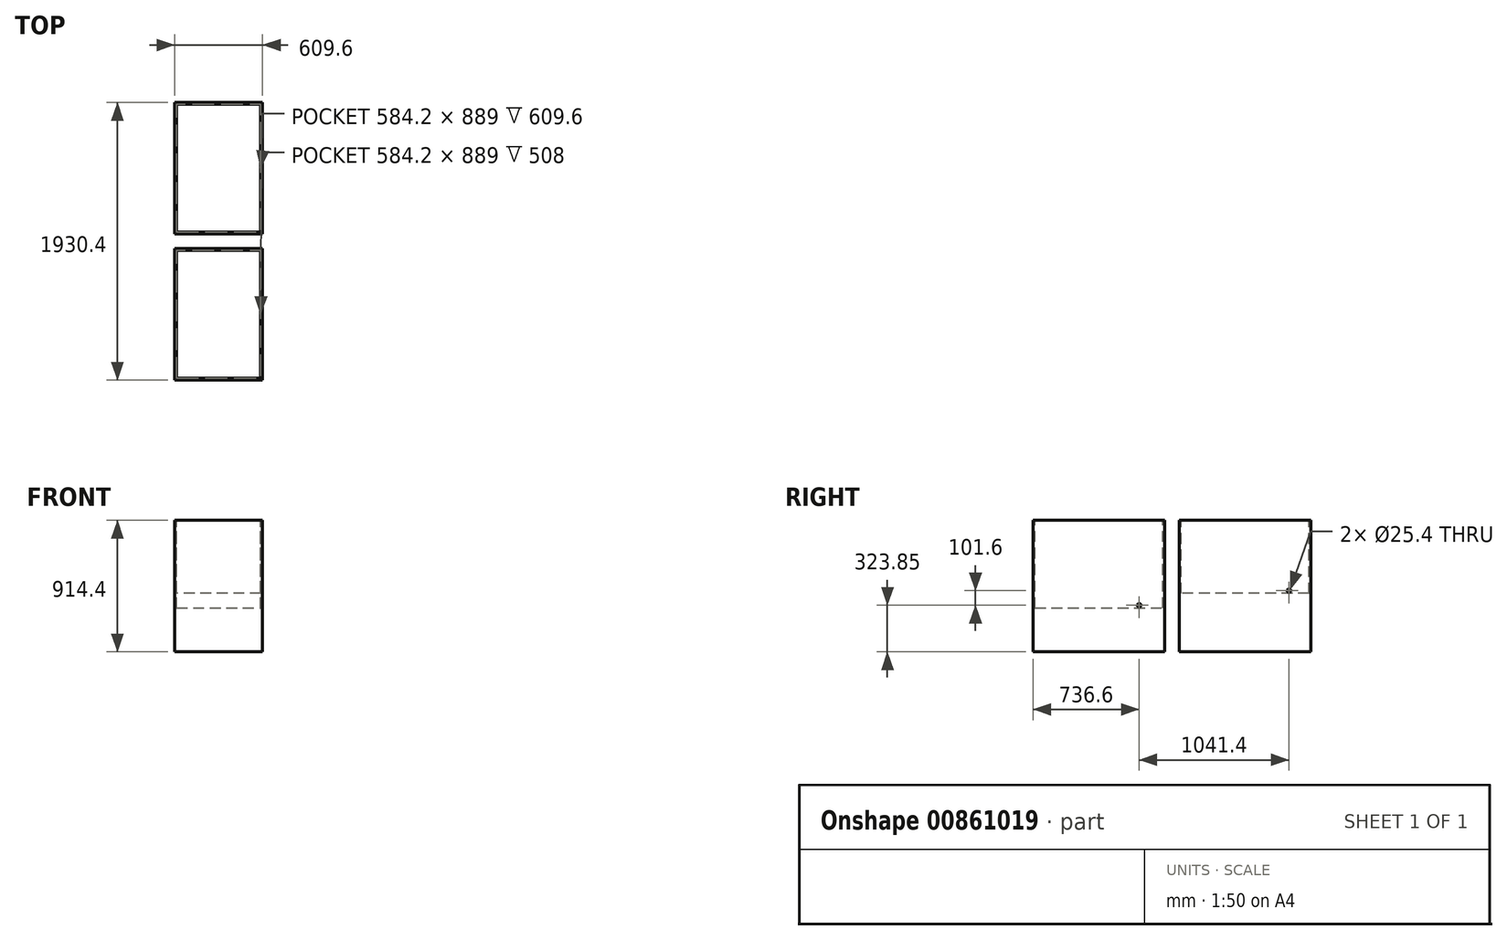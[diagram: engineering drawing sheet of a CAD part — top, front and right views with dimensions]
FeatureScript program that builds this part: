
annotation { "Feature Type Name" : "Feature", "Feature Type Description" : "" }
export const myFeature = defineFeature(function(context is Context, id is Id, definition is map)
    precondition{}
    {
        {
            var Q0;
            Q0=qCreatedBy(makeId("Top.planeOp"),FACE);
            var sketch = newSketch(context, id + "F0", { "sketchPlane" : qUnion([Q0])});
            skLineSegment(sketch, "E0.bottom", {"start": v(304.8, 457.2) * mm, "end": v(-304.8, 457.2) * mm});
            skLineSegment(sketch, "E0.top", {"start": v(304.8, -457.2) * mm, "end": v(-304.8, -457.2) * mm});
            skLineSegment(sketch, "E0.left", {"start": v(304.8, 457.2) * mm, "end": v(304.8, -457.2) * mm});
            skLineSegment(sketch, "E0.right", {"start": v(-304.8, 457.2) * mm, "end": v(-304.8, -457.2) * mm});
            skPoint(sketch, "E0.middle", {"position": v(0, 0) * mm});
            skSolve(sketch);
        }
        {
            var Q0;
            Q0=makeQuery(id+"F0.imprint","IMPRINT",FACE,{"disambiguationData":[TD([[makeQuery(id+"F0.imprint","IMPRINT",EDGE,{"derivedFrom":sQuery(id+"F0.wireOp",EDGE,"E0.bottom")}),1.0]])]});
            extrude(context, id + "F1", {"entities" : qUnion([Q0]), "depth" : 914.4 * mm, "offsetDistance" : 25.4 * mm});
        }
        {
            var Q0;
            Q0=qCreatedBy(makeId("Top.planeOp"),FACE);
            var sketch = newSketch(context, id + "F2", { "sketchPlane" : qUnion([Q0])});
            skLineSegment(sketch, "E1.bottom", {"start": v(-304.8, -558.8) * mm, "end": v(304.8, -558.8) * mm});
            skLineSegment(sketch, "E1.top", {"start": v(-304.8, -1473.2) * mm, "end": v(304.8, -1473.2) * mm});
            skLineSegment(sketch, "E1.left", {"start": v(-304.8, -558.8) * mm, "end": v(-304.8, -1473.2) * mm});
            skLineSegment(sketch, "E1.right", {"start": v(304.8, -558.8) * mm, "end": v(304.8, -1473.2) * mm});
            skSolve(sketch);
        }
        {
            var Q0;
            Q0 = qSketchRegion(id + "F2", true);
            extrude(context, id + "F3", {"entities" : qUnion([Q0]), "depth" : 914.4 * mm, "offsetDistance" : 25.4 * mm});
        }
        {
            var Q0;
            Q0=makeQuery(id+"F1.opExtrude","CAP_FACE",FACE,{"disambiguationData":[OSD([sQuery(id+"F0.wireOp",EDGE,"E0.bottom"),sQuery(id+"F0.wireOp",EDGE,"E0.top"),sQuery(id+"F0.wireOp",EDGE,"E0.left"),sQuery(id+"F0.wireOp",EDGE,"E0.right")])],"isStart":false});
            var sketch = newSketch(context, id + "F4", { "sketchPlane" : qUnion([Q0])});
            skLineSegment(sketch, "E2.bottom", {"start": v(292.1, 444.5) * mm, "end": v(-292.1, 444.5) * mm});
            skLineSegment(sketch, "E2.top", {"start": v(292.1, -444.5) * mm, "end": v(-292.1, -444.5) * mm});
            skLineSegment(sketch, "E2.left", {"start": v(292.1, 444.5) * mm, "end": v(292.1, -444.5) * mm});
            skLineSegment(sketch, "E2.right", {"start": v(-292.1, 444.5) * mm, "end": v(-292.1, -444.5) * mm});
            skPoint(sketch, "E2.middle", {"position": v(0, 0) * mm});
            skSolve(sketch);
        }
        {
            var Q0;
            Q0=makeQuery(id+"F4.imprint","IMPRINT",FACE,{"disambiguationData":[TD([[makeQuery(id+"F4.imprint","IMPRINT",EDGE,{"derivedFrom":sQuery(id+"F4.wireOp",EDGE,"E2.bottom")}),1.0]])]});
            extrude(context, id + "F5", {"entities" : qUnion([Q0]), "operationType" : NewBodyOperationType.REMOVE, "oppositeDirection" : true, "depth" : 508 * mm, "offsetDistance" : 25.4 * mm});
        }
        {
            var Q0;
            Q0=makeQuery(id+"F3.opExtrude","CAP_FACE",FACE,{"disambiguationData":[OSD([sQuery(id+"F2.wireOp",EDGE,"E1.bottom"),sQuery(id+"F2.wireOp",EDGE,"E1.top"),sQuery(id+"F2.wireOp",EDGE,"E1.left"),sQuery(id+"F2.wireOp",EDGE,"E1.right")])],"isStart":false});
            var sketch = newSketch(context, id + "F6", { "sketchPlane" : qUnion([Q0])});
            skLineSegment(sketch, "E3.bottom", {"start": v(-292.1, -1460.5) * mm, "end": v(292.1, -1460.5) * mm});
            skLineSegment(sketch, "E3.top", {"start": v(-292.1, -571.5) * mm, "end": v(292.1, -571.5) * mm});
            skLineSegment(sketch, "E3.left", {"start": v(-292.1, -1460.5) * mm, "end": v(-292.1, -571.5) * mm});
            skLineSegment(sketch, "E3.right", {"start": v(292.1, -1460.5) * mm, "end": v(292.1, -571.5) * mm});
            skSolve(sketch);
        }
        {
            var Q0;
            Q0=makeQuery(id+"F6.imprint","IMPRINT",FACE,{"disambiguationData":[TD([[makeQuery(id+"F6.imprint","IMPRINT",EDGE,{"derivedFrom":sQuery(id+"F6.wireOp",EDGE,"E3.bottom")}),1.0]])]});
            extrude(context, id + "F7", {"entities" : qUnion([Q0]), "operationType" : NewBodyOperationType.REMOVE, "oppositeDirection" : true, "depth" : 609.6 * mm, "offsetDistance" : 25.4 * mm});
        }
        {
            var Q0;
            Q0=makeQuery(id+"F1.opExtrude","SWEPT_FACE",FACE,{"disambiguationData":[OSD([sQuery(id+"F0.wireOp",EDGE,"E0.left")])]});
            var sketch = newSketch(context, id + "F8", { "sketchPlane" : qUnion([Q0])});
            skCircle(sketch, "E4", {"center": v(304.8, 425.45) * mm, "radius": 12.7 * mm});
            skSolve(sketch);
        }
        {
            var Q0;
            Q0 = qSketchRegion(id + "F8", true);
            extrude(context, id + "F9", {"entities" : qUnion([Q0]), "operationType" : NewBodyOperationType.REMOVE, "oppositeDirection" : true, "depth" : 25.4 * mm, "offsetDistance" : 25.4 * mm});
        }
        {
            var Q0;
            Q0=makeQuery(id+"F3.opExtrude","SWEPT_FACE",FACE,{"disambiguationData":[OSD([sQuery(id+"F2.wireOp",EDGE,"E1.right")])]});
            var sketch = newSketch(context, id + "F10", { "sketchPlane" : qUnion([Q0])});
            skCircle(sketch, "E5", {"center": v(-736.6, 323.85) * mm, "radius": 12.7 * mm});
            skSolve(sketch);
        }
        {
            var Q0;
            Q0 = qSketchRegion(id + "F10", true);
            extrude(context, id + "F11", {"entities" : qUnion([Q0]), "operationType" : NewBodyOperationType.REMOVE, "oppositeDirection" : true, "depth" : 25.4 * mm, "offsetDistance" : 25.4 * mm});
        }
    });
